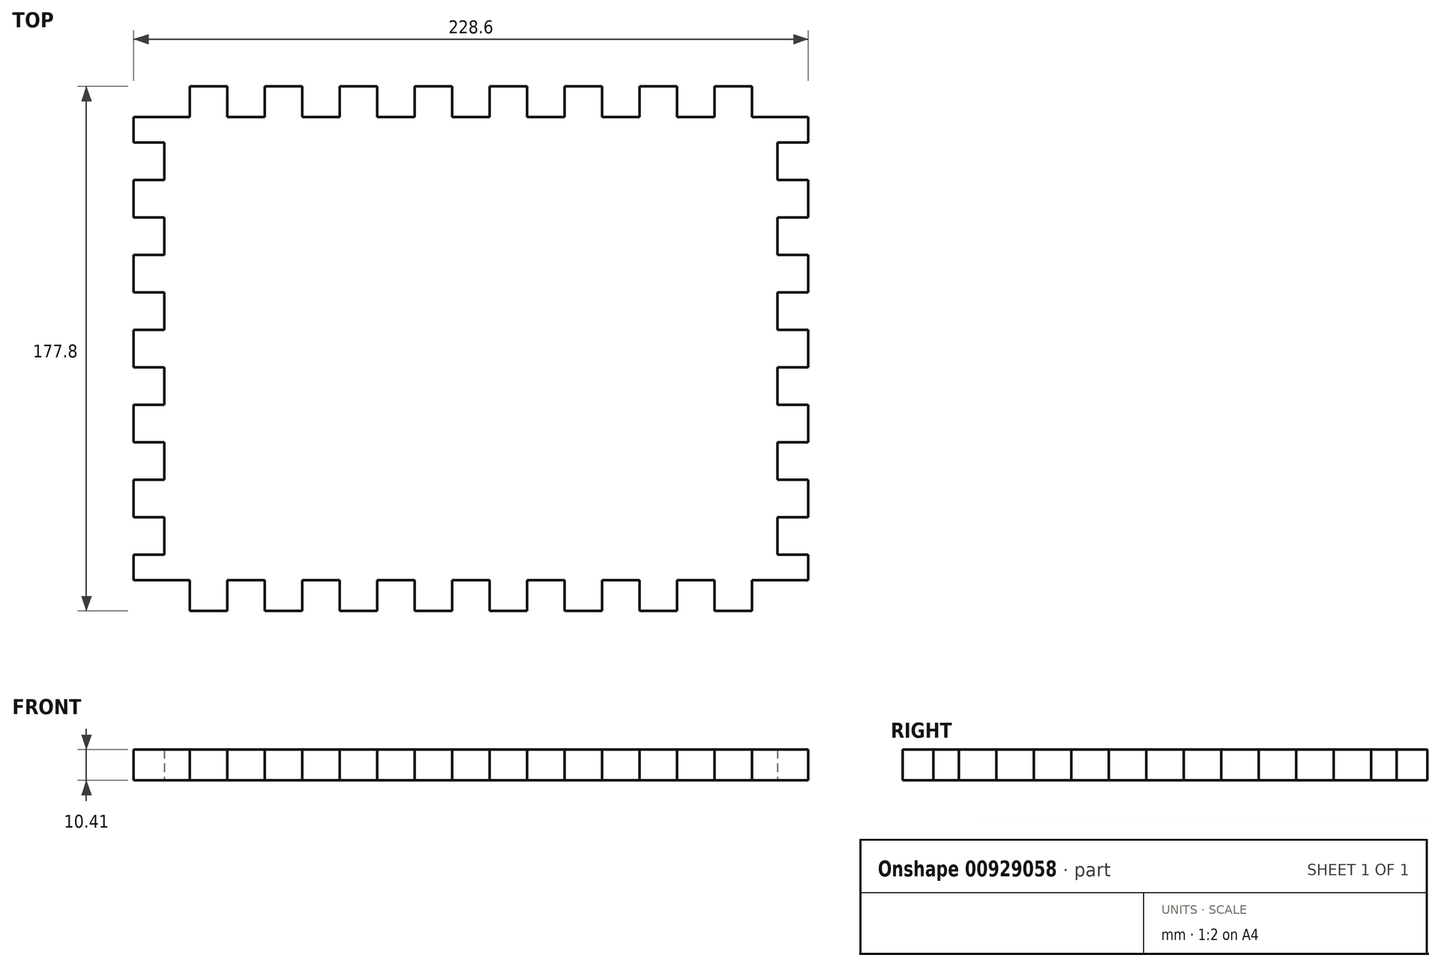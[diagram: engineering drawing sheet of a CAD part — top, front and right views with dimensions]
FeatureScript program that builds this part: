
annotation { "Feature Type Name" : "Feature", "Feature Type Description" : "" }
export const myFeature = defineFeature(function(context is Context, id is Id, definition is map)
    precondition{}
    {
        {
            var Q0;
            Q0=qCreatedBy(makeId("Top.planeOp"),FACE);
            var sketch = newSketch(context, id + "F0", { "sketchPlane" : qUnion([Q0])});
            skLineSegment(sketch, "E0.bottom", {"start": v(19.05, 0) * mm, "end": v(31.75, 0) * mm});
            skLineSegment(sketch, "E0.left", {"start": v(0, -10.41) * mm, "end": v(0, -19.05) * mm});
            skLineSegment(sketch, "E1", {"start": v(0, -10.41) * mm, "end": v(19.05, -10.41) * mm});
            skLineSegment(sketch, "E2", {"start": v(19.05, -10.41) * mm, "end": v(19.05, 0) * mm});
            skLineSegment(sketch, "E3", {"start": v(31.75, 0) * mm, "end": v(31.75, -10.41) * mm});
            skLineSegment(sketch, "E4", {"start": v(31.75, -10.41) * mm, "end": v(44.45, -10.41) * mm});
            skLineSegment(sketch, "E5", {"start": v(44.45, -10.41) * mm, "end": v(44.45, 0) * mm});
            skLineSegment(sketch, "E6", {"start": v(44.45, 0) * mm, "end": v(57.15, 0) * mm});
            skLineSegment(sketch, "E7", {"start": v(57.15, 0) * mm, "end": v(57.15, -10.41) * mm});
            skLineSegment(sketch, "E8", {"start": v(57.15, -10.41) * mm, "end": v(69.85, -10.41) * mm});
            skLineSegment(sketch, "E9", {"start": v(69.85, -10.41) * mm, "end": v(69.85, 0) * mm});
            skPoint(sketch, "E10.orphan", {"position": v(0, 0) * mm});
            skLineSegment(sketch, "E11.trimOffspring", {"start": v(69.85, 0) * mm, "end": v(82.55, 0) * mm});
            skLineSegment(sketch, "E12", {"start": v(82.55, 0) * mm, "end": v(82.55, -10.41) * mm});
            skLineSegment(sketch, "E13", {"start": v(82.55, -10.41) * mm, "end": v(95.25, -10.41) * mm});
            skLineSegment(sketch, "E14", {"start": v(95.25, -10.41) * mm, "end": v(95.25, 0) * mm});
            skLineSegment(sketch, "E15", {"start": v(95.25, 0) * mm, "end": v(107.95, 0) * mm});
            skLineSegment(sketch, "E16", {"start": v(107.95, 0) * mm, "end": v(107.95, -10.41) * mm});
            skLineSegment(sketch, "E17", {"start": v(107.95, -10.41) * mm, "end": v(120.65, -10.41) * mm});
            skLineSegment(sketch, "E18", {"start": v(120.65, -10.41) * mm, "end": v(120.65, 0) * mm});
            skLineSegment(sketch, "E19", {"start": v(120.65, 0) * mm, "end": v(133.35, 0) * mm});
            skLineSegment(sketch, "E20", {"start": v(133.35, 0) * mm, "end": v(133.35, -10.41) * mm});
            skLineSegment(sketch, "E21", {"start": v(133.35, -10.41) * mm, "end": v(146.05, -10.41) * mm});
            skLineSegment(sketch, "E22", {"start": v(146.05, -10.41) * mm, "end": v(146.05, 0) * mm});
            skLineSegment(sketch, "E23.trimOffspring", {"start": v(146.05, 0) * mm, "end": v(158.75, 0) * mm});
            skLineSegment(sketch, "E24", {"start": v(158.75, 0) * mm, "end": v(158.75, -10.41) * mm});
            skLineSegment(sketch, "E25", {"start": v(158.75, -10.41) * mm, "end": v(171.45, -10.41) * mm});
            skLineSegment(sketch, "E26", {"start": v(171.45, -10.41) * mm, "end": v(171.45, 0) * mm});
            skLineSegment(sketch, "E27", {"start": v(171.45, 0) * mm, "end": v(184.15, 0) * mm});
            skLineSegment(sketch, "E28", {"start": v(184.15, 0) * mm, "end": v(184.15, -10.41) * mm});
            skLineSegment(sketch, "E29", {"start": v(184.15, -10.41) * mm, "end": v(196.85, -10.41) * mm});
            skLineSegment(sketch, "E30", {"start": v(196.85, -10.41) * mm, "end": v(196.85, 0) * mm});
            skLineSegment(sketch, "E31.trimOffspring", {"start": v(196.85, 0) * mm, "end": v(209.55, 0) * mm});
            skLineSegment(sketch, "E32", {"start": v(209.55, 0) * mm, "end": v(209.55, -10.41) * mm});
            skLineSegment(sketch, "E33", {"start": v(209.55, -10.41) * mm, "end": v(228.6, -10.41) * mm});
            skPoint(sketch, "E34.orphan", {"position": v(228.6, 0) * mm});
            skLineSegment(sketch, "E35", {"start": v(0, -19.05) * mm, "end": v(10.41, -19.05) * mm});
            skLineSegment(sketch, "E36", {"start": v(10.41, -19.05) * mm, "end": v(10.41, -31.75) * mm});
            skLineSegment(sketch, "E37", {"start": v(10.41, -31.75) * mm, "end": v(0, -31.75) * mm});
            skLineSegment(sketch, "E38", {"start": v(0, -31.75) * mm, "end": v(0, -44.45) * mm});
            skLineSegment(sketch, "E39", {"start": v(0, -44.45) * mm, "end": v(10.41, -44.45) * mm});
            skLineSegment(sketch, "E40", {"start": v(10.41, -44.45) * mm, "end": v(10.41, -57.15) * mm});
            skLineSegment(sketch, "E41", {"start": v(10.41, -57.15) * mm, "end": v(0, -57.15) * mm});
            skLineSegment(sketch, "E42", {"start": v(0, -57.15) * mm, "end": v(0, -69.85) * mm});
            skLineSegment(sketch, "E43", {"start": v(0, -69.85) * mm, "end": v(10.41, -69.85) * mm});
            skLineSegment(sketch, "E44", {"start": v(10.41, -69.85) * mm, "end": v(10.41, -82.55) * mm});
            skLineSegment(sketch, "E45", {"start": v(10.41, -82.55) * mm, "end": v(0, -82.55) * mm});
            skLineSegment(sketch, "E46.trimOffspring", {"start": v(0, -82.55) * mm, "end": v(0, -95.25) * mm});
            skLineSegment(sketch, "E47", {"start": v(0, -95.25) * mm, "end": v(10.41, -95.25) * mm});
            skLineSegment(sketch, "E48", {"start": v(10.41, -95.25) * mm, "end": v(10.41, -107.95) * mm});
            skLineSegment(sketch, "E49", {"start": v(10.41, -107.95) * mm, "end": v(0, -107.95) * mm});
            skLineSegment(sketch, "E50", {"start": v(0, -107.95) * mm, "end": v(0, -120.65) * mm});
            skLineSegment(sketch, "E51", {"start": v(0, -120.65) * mm, "end": v(10.41, -120.65) * mm});
            skLineSegment(sketch, "E52", {"start": v(10.41, -120.65) * mm, "end": v(10.41, -133.35) * mm});
            skLineSegment(sketch, "E53", {"start": v(10.41, -133.35) * mm, "end": v(0, -133.35) * mm});
            skLineSegment(sketch, "E54.trimOffspring", {"start": v(0, -133.35) * mm, "end": v(0, -146.05) * mm});
            skLineSegment(sketch, "E55", {"start": v(0, -146.05) * mm, "end": v(10.41, -146.05) * mm});
            skLineSegment(sketch, "E56", {"start": v(10.41, -146.05) * mm, "end": v(10.41, -158.75) * mm});
            skLineSegment(sketch, "E57", {"start": v(10.41, -158.75) * mm, "end": v(0, -158.75) * mm});
            skLineSegment(sketch, "E58", {"start": v(0, -158.75) * mm, "end": v(0, -167.39) * mm});
            skLineSegment(sketch, "E59", {"start": v(0, -167.39) * mm, "end": v(19.05, -167.39) * mm});
            skLineSegment(sketch, "E60", {"start": v(19.05, -167.39) * mm, "end": v(19.05, -177.8) * mm});
            skPoint(sketch, "E61.orphan", {"position": v(0, -177.8) * mm});
            skLineSegment(sketch, "E62", {"start": v(114.3, -10.41) * mm, "end": v(114.3, -10.41) * mm});
            skLineSegment(sketch, "E63", {"start": v(0, -88.9) * mm, "end": v(0, -88.9) * mm});
            skLineSegment(sketch, "E64.MirrorCS", {"start": v(228.6, -158.75) * mm, "end": v(228.6, -167.39) * mm});
            skLineSegment(sketch, "E65.MirrorCS", {"start": v(228.6, -10.41) * mm, "end": v(228.6, -19.05) * mm});
            skLineSegment(sketch, "E66.MirrorCS", {"start": v(228.6, -19.05) * mm, "end": v(218.19, -19.05) * mm});
            skLineSegment(sketch, "E67.MirrorCS", {"start": v(228.6, -44.45) * mm, "end": v(218.19, -44.45) * mm});
            skLineSegment(sketch, "E68.MirrorCS", {"start": v(218.19, -133.35) * mm, "end": v(228.6, -133.35) * mm});
            skLineSegment(sketch, "E69.MirrorCS", {"start": v(228.6, -146.05) * mm, "end": v(218.19, -146.05) * mm});
            skLineSegment(sketch, "E70.MirrorCS", {"start": v(228.6, -69.85) * mm, "end": v(218.19, -69.85) * mm});
            skLineSegment(sketch, "E71.MirrorCS", {"start": v(228.6, -95.25) * mm, "end": v(218.19, -95.25) * mm});
            skLineSegment(sketch, "E72.MirrorCS", {"start": v(218.19, -107.95) * mm, "end": v(228.6, -107.95) * mm});
            skLineSegment(sketch, "E73.MirrorCS", {"start": v(228.6, -82.55) * mm, "end": v(228.6, -95.25) * mm});
            skLineSegment(sketch, "E74.MirrorCS", {"start": v(218.19, -158.75) * mm, "end": v(228.6, -158.75) * mm});
            skLineSegment(sketch, "E75.MirrorCS", {"start": v(218.19, -57.15) * mm, "end": v(228.6, -57.15) * mm});
            skLineSegment(sketch, "E76.MirrorCS", {"start": v(228.6, -120.65) * mm, "end": v(218.19, -120.65) * mm});
            skLineSegment(sketch, "E77.MirrorCS", {"start": v(218.19, -82.55) * mm, "end": v(228.6, -82.55) * mm});
            skLineSegment(sketch, "E78.MirrorCS", {"start": v(218.19, -31.75) * mm, "end": v(228.6, -31.75) * mm});
            skLineSegment(sketch, "E79.MirrorCS", {"start": v(209.55, -167.39) * mm, "end": v(209.55, -177.8) * mm});
            skLineSegment(sketch, "E80.MirrorCS", {"start": v(228.6, -31.75) * mm, "end": v(228.6, -44.45) * mm});
            skLineSegment(sketch, "E81.MirrorCS", {"start": v(228.6, -107.95) * mm, "end": v(228.6, -120.65) * mm});
            skLineSegment(sketch, "E82.MirrorCS", {"start": v(218.19, -19.05) * mm, "end": v(218.19, -31.75) * mm});
            skLineSegment(sketch, "E83.MirrorCS", {"start": v(228.6, -57.15) * mm, "end": v(228.6, -69.85) * mm});
            skLineSegment(sketch, "E84.MirrorCS", {"start": v(228.6, -133.35) * mm, "end": v(228.6, -146.05) * mm});
            skLineSegment(sketch, "E85.MirrorCS", {"start": v(218.19, -146.05) * mm, "end": v(218.19, -158.75) * mm});
            skLineSegment(sketch, "E86.MirrorCS", {"start": v(218.19, -120.65) * mm, "end": v(218.19, -133.35) * mm});
            skLineSegment(sketch, "E87.MirrorCS", {"start": v(218.19, -44.45) * mm, "end": v(218.19, -57.15) * mm});
            skLineSegment(sketch, "E88.MirrorCS", {"start": v(228.6, -10.41) * mm, "end": v(209.55, -10.41) * mm});
            skLineSegment(sketch, "E89.MirrorCS", {"start": v(228.6, -167.39) * mm, "end": v(209.55, -167.39) * mm});
            skLineSegment(sketch, "E90.MirrorCS", {"start": v(218.19, -95.25) * mm, "end": v(218.19, -107.95) * mm});
            skLineSegment(sketch, "E91.MirrorCS", {"start": v(218.19, -69.85) * mm, "end": v(218.19, -82.55) * mm});
            skLineSegment(sketch, "E92.MirrorCS", {"start": v(171.45, -177.8) * mm, "end": v(184.15, -177.8) * mm});
            skLineSegment(sketch, "E93.MirrorCS", {"start": v(69.85, -177.8) * mm, "end": v(82.55, -177.8) * mm});
            skLineSegment(sketch, "E94.MirrorCS", {"start": v(107.95, -167.39) * mm, "end": v(120.65, -167.39) * mm});
            skLineSegment(sketch, "E95.MirrorCS", {"start": v(19.05, -177.8) * mm, "end": v(31.75, -177.8) * mm});
            skLineSegment(sketch, "E96.MirrorCS", {"start": v(146.05, -177.8) * mm, "end": v(158.75, -177.8) * mm});
            skLineSegment(sketch, "E97.MirrorCS", {"start": v(196.85, -177.8) * mm, "end": v(209.55, -177.8) * mm});
            skLineSegment(sketch, "E98.MirrorCS", {"start": v(120.65, -177.8) * mm, "end": v(133.35, -177.8) * mm});
            skLineSegment(sketch, "E99.MirrorCS", {"start": v(44.45, -177.8) * mm, "end": v(57.15, -177.8) * mm});
            skLineSegment(sketch, "E100.MirrorCS", {"start": v(158.75, -167.39) * mm, "end": v(171.45, -167.39) * mm});
            skLineSegment(sketch, "E101.MirrorCS", {"start": v(82.55, -177.8) * mm, "end": v(82.55, -167.39) * mm});
            skLineSegment(sketch, "E102.MirrorCS", {"start": v(133.35, -177.8) * mm, "end": v(133.35, -167.39) * mm});
            skLineSegment(sketch, "E103.MirrorCS", {"start": v(82.55, -167.39) * mm, "end": v(95.25, -167.39) * mm});
            skLineSegment(sketch, "E104.MirrorCS", {"start": v(57.15, -167.39) * mm, "end": v(69.85, -167.39) * mm});
            skLineSegment(sketch, "E105.MirrorCS", {"start": v(184.15, -167.39) * mm, "end": v(196.85, -167.39) * mm});
            skLineSegment(sketch, "E106.MirrorCS", {"start": v(107.95, -177.8) * mm, "end": v(107.95, -167.39) * mm});
            skLineSegment(sketch, "E107.MirrorCS", {"start": v(184.15, -177.8) * mm, "end": v(184.15, -167.39) * mm});
            skLineSegment(sketch, "E108.MirrorCS", {"start": v(158.75, -177.8) * mm, "end": v(158.75, -167.39) * mm});
            skLineSegment(sketch, "E109.MirrorCS", {"start": v(120.65, -167.39) * mm, "end": v(120.65, -177.8) * mm});
            skLineSegment(sketch, "E110.MirrorCS", {"start": v(95.25, -167.39) * mm, "end": v(95.25, -177.8) * mm});
            skLineSegment(sketch, "E111.MirrorCS", {"start": v(196.85, -167.39) * mm, "end": v(196.85, -177.8) * mm});
            skLineSegment(sketch, "E112.MirrorCS", {"start": v(44.45, -167.39) * mm, "end": v(44.45, -177.8) * mm});
            skLineSegment(sketch, "E113.MirrorCS", {"start": v(31.75, -167.39) * mm, "end": v(44.45, -167.39) * mm});
            skLineSegment(sketch, "E114.MirrorCS", {"start": v(133.35, -167.39) * mm, "end": v(146.05, -167.39) * mm});
            skLineSegment(sketch, "E115.MirrorCS", {"start": v(69.85, -167.39) * mm, "end": v(69.85, -177.8) * mm});
            skLineSegment(sketch, "E116.MirrorCS", {"start": v(146.05, -167.39) * mm, "end": v(146.05, -177.8) * mm});
            skLineSegment(sketch, "E117.MirrorCS", {"start": v(171.45, -167.39) * mm, "end": v(171.45, -177.8) * mm});
            skLineSegment(sketch, "E118.MirrorCS", {"start": v(95.25, -177.8) * mm, "end": v(107.95, -177.8) * mm});
            skLineSegment(sketch, "E119.MirrorCS", {"start": v(57.15, -177.8) * mm, "end": v(57.15, -167.39) * mm});
            skLineSegment(sketch, "E120.MirrorCS", {"start": v(209.55, -177.8) * mm, "end": v(209.55, -167.39) * mm});
            skLineSegment(sketch, "E121.MirrorCS", {"start": v(31.75, -177.8) * mm, "end": v(31.75, -167.39) * mm});
            skSolve(sketch);
        }
        {
            var Q0;
            Q0=makeQuery(id+"F0.imprint","IMPRINT",FACE,{"disambiguationData":[TD([[makeQuery(id+"F0.imprint","IMPRINT",EDGE,{"derivedFrom":sQuery(id+"F0.wireOp",EDGE,"E1")}),-1.0]])]});
            extrude(context, id + "F1", {"entities" : qUnion([Q0]), "depth" : 10.4 * mm, "offsetDistance" : 25.4 * mm});
        }
    });
